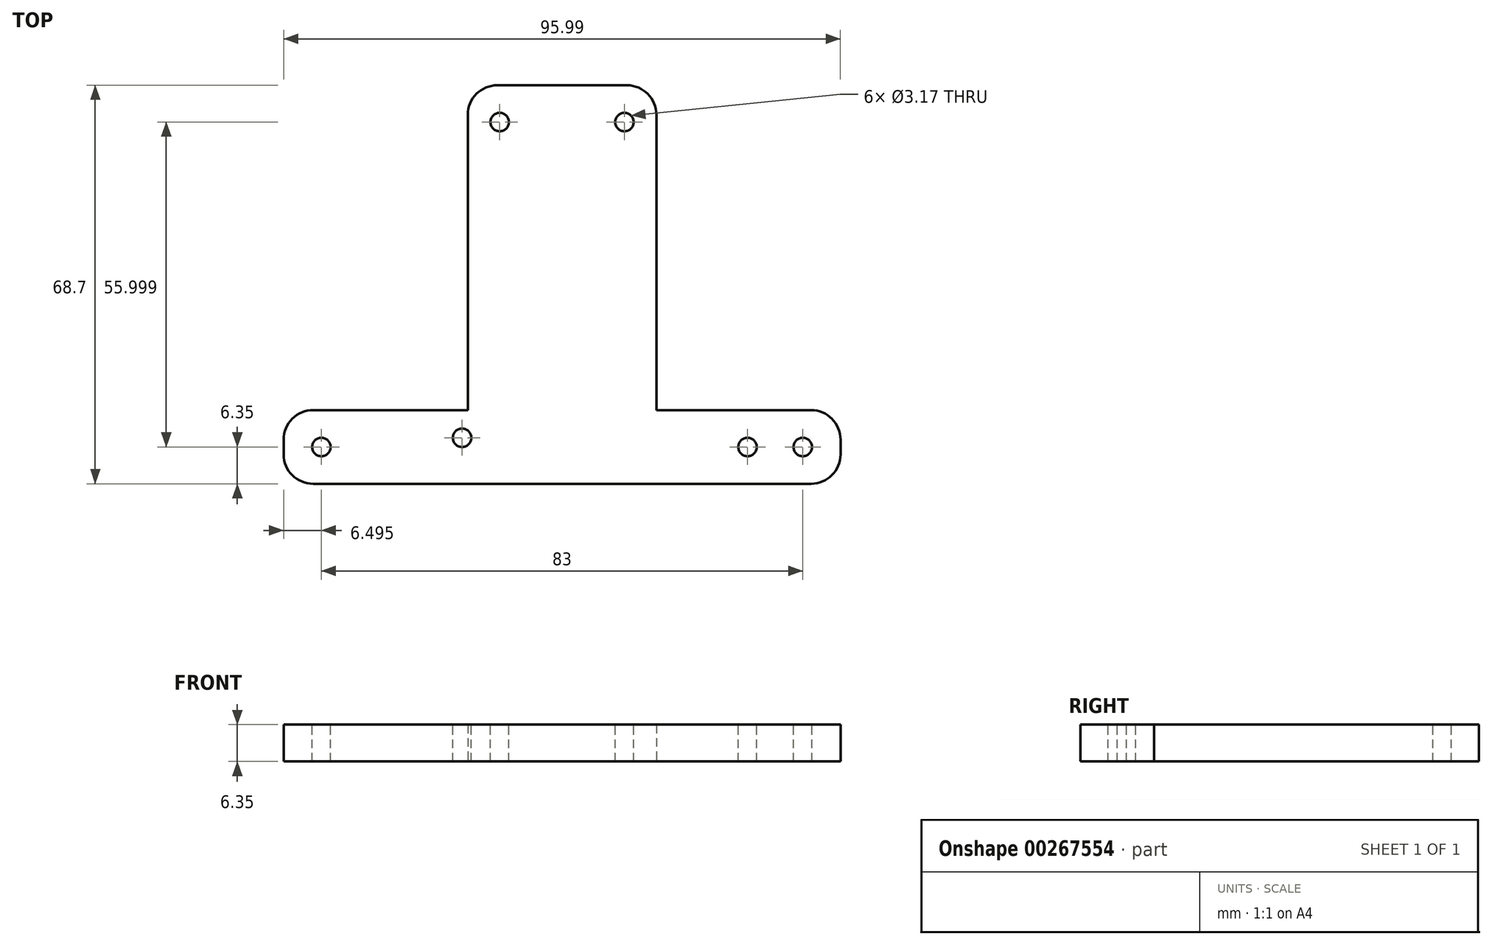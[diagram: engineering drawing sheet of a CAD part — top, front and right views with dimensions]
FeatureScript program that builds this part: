
annotation { "Feature Type Name" : "Feature", "Feature Type Description" : "" }
export const myFeature = defineFeature(function(context is Context, id is Id, definition is map)
    precondition{}
    {
        {
            var Q0;
            Q0=qCreatedBy(makeId("Top.planeOp"),FACE);
            var sketch = newSketch(context, id + "F0", { "sketchPlane" : qUnion([Q0])});
            skLineSegment(sketch, "E0.bottom", {"start": v(-48.42, 0) * mm, "end": v(47.57, 0) * mm});
            skLineSegment(sketch, "E0.top", {"start": v(-48.42, 12.7) * mm, "end": v(47.57, 12.7) * mm});
            skLineSegment(sketch, "E0.left", {"start": v(-48.42, 0) * mm, "end": v(-48.42, 12.7) * mm});
            skLineSegment(sketch, "E0.right", {"start": v(47.57, 0) * mm, "end": v(47.57, 12.7) * mm});
            skLineSegment(sketch, "E1.bottom", {"start": v(-16.67, 12.7) * mm, "end": v(15.82, 12.7) * mm});
            skLineSegment(sketch, "E1.top", {"start": v(-16.67, 68.7) * mm, "end": v(15.82, 68.7) * mm});
            skLineSegment(sketch, "E1.left", {"start": v(-16.67, 12.7) * mm, "end": v(-16.67, 68.7) * mm});
            skLineSegment(sketch, "E1.right", {"start": v(15.82, 12.7) * mm, "end": v(15.82, 68.7) * mm});
            skSolve(sketch);
        }
        {
            var Q0;
            Q0 = qSketchRegion(id + "F0", true);
            extrude(context, id + "F1", {"entities" : qUnion([Q0]), "depth" : 6.35 * mm});
        }
        {
            var Q0;
            Q0=makeQuery(id+"F1.opExtrude","CAP_FACE",FACE,{"disambiguationData":[OSD([sQuery(id+"F0.wireOp",EDGE,"E0.bottom"),sQuery(id+"F0.wireOp",EDGE,"E0.top"),sQuery(id+"F0.wireOp",EDGE,"E0.left"),sQuery(id+"F0.wireOp",EDGE,"E0.right"),sQuery(id+"F0.wireOp",EDGE,"E1.top"),sQuery(id+"F0.wireOp",EDGE,"E1.left"),sQuery(id+"F0.wireOp",EDGE,"E1.right")])],"isStart":false});
            var sketch = newSketch(context, id + "F2", { "sketchPlane" : qUnion([Q0])});
            skCircle(sketch, "E2", {"center": v(41.08, 6.35) * mm, "radius": 1.59 * mm});
            skCircle(sketch, "E3", {"center": v(-41.92, 6.35) * mm, "radius": 1.59 * mm});
            skCircle(sketch, "E4", {"center": v(-11.18, 62.35) * mm, "radius": 1.59 * mm});
            skCircle(sketch, "E5", {"center": v(10.33, 62.35) * mm, "radius": 1.59 * mm});
            skSolve(sketch);
        }
        {
            var Q0;
            Q0 = qSketchRegion(id + "F2", true);
            extrude(context, id + "F3", {"entities" : qUnion([Q0]), "operationType" : NewBodyOperationType.REMOVE, "oppositeDirection" : true, "depth" : 25.4 * mm});
        }
        {
            var Q0;
            Q0=makeQuery(id+"F1.opExtrude","SWEPT_EDGE",EDGE,{"disambiguationData":[OSD([sQuery(id+"F0.wireOp",EDGE,"E0.top"),sQuery(id+"F0.wireOp",EDGE,"E0.right")])]});
            var Q1;
            Q1=makeQuery(id+"F1.opExtrude","SWEPT_EDGE",EDGE,{"disambiguationData":[OSD([sQuery(id+"F0.wireOp",EDGE,"E0.bottom"),sQuery(id+"F0.wireOp",EDGE,"E0.right")])]});
            var Q2;
            Q2=makeQuery(id+"F1.opExtrude","SWEPT_EDGE",EDGE,{"disambiguationData":[OSD([sQuery(id+"F0.wireOp",EDGE,"E0.bottom"),sQuery(id+"F0.wireOp",EDGE,"E0.left")])]});
            var Q3;
            Q3=makeQuery(id+"F1.opExtrude","SWEPT_EDGE",EDGE,{"disambiguationData":[OSD([sQuery(id+"F0.wireOp",EDGE,"E0.top"),sQuery(id+"F0.wireOp",EDGE,"E0.left")])]});
            var Q4;
            Q4=makeQuery(id+"F1.opExtrude","SWEPT_EDGE",EDGE,{"disambiguationData":[OSD([sQuery(id+"F0.wireOp",EDGE,"E1.top"),sQuery(id+"F0.wireOp",EDGE,"E1.right")])]});
            var Q5;
            Q5=makeQuery(id+"F1.opExtrude","SWEPT_EDGE",EDGE,{"disambiguationData":[OSD([sQuery(id+"F0.wireOp",EDGE,"E1.top"),sQuery(id+"F0.wireOp",EDGE,"E1.left")])]});
            fillet(context, id + "F4", {"entities" : qUnion([Q0, Q1, Q2, Q3, Q4, Q5]), "radius" : 5.08 * mm, "tangentPropagation" : true, "allowEdgeOverflow" : false});
        }
        {
            var Q0;
            Q0=makeQuery(id+"F1.opExtrude","CAP_FACE",FACE,{"disambiguationData":[OSD([sQuery(id+"F0.wireOp",EDGE,"E0.bottom"),sQuery(id+"F0.wireOp",EDGE,"E0.top"),sQuery(id+"F0.wireOp",EDGE,"E0.left"),sQuery(id+"F0.wireOp",EDGE,"E0.right"),sQuery(id+"F0.wireOp",EDGE,"E1.top"),sQuery(id+"F0.wireOp",EDGE,"E1.left"),sQuery(id+"F0.wireOp",EDGE,"E1.right")])],"isStart":false});
            var sketch = newSketch(context, id + "F5", { "sketchPlane" : qUnion([Q0])});
            skCircle(sketch, "E6", {"center": v(31.55, 6.35) * mm, "radius": 1.59 * mm});
            skCircle(sketch, "E7", {"center": v(-17.66, 7.94) * mm, "radius": 1.59 * mm});
            skLineSegment(sketch, "E8", {"start": v(31.55, 6.35) * mm, "end": v(-31.22, 6.35) * mm});
            skLineSegment(sketch, "E9", {"start": v(-16.07, 7.94) * mm, "end": v(-16.07, 6.35) * mm});
            skSolve(sketch);
        }
        {
            var Q0;
            {var subQ0=sQuery(id+"F5.wireOp",EDGE,"E7");var subQ1=makeQuery(id+"F5.imprint","INTERSECT",VERTEX,{"derivedFrom":[subQ0,sQuery(id+"F5.wireOp",EDGE,"E9")]});Q0=makeQuery(id+"F5.imprint","IMPRINT",FACE,{"disambiguationData":[TD([[makeQuery(id+"F5.imprint","IMPRINT",EDGE,{"disambiguationData":[TD([[subQ1,-1.0]])],"derivedFrom":subQ0}),1.0]])]});}
            var Q1;
            Q1=makeQuery(id+"F5.imprint","IMPRINT",FACE,{"disambiguationData":[TD([[makeQuery(id+"F5.imprint","IMPRINT",EDGE,{"derivedFrom":sQuery(id+"F5.wireOp",EDGE,"E6")}),1.0]])]});
            var Q2;
            Q2=sQuery(id+"F5.wireOp",EDGE,"E7");
            var Q3;
            Q3=sQuery(id+"F5.wireOp",EDGE,"E6");
            extrude(context, id + "F6", {"entities" : qUnion([Q0, Q1]), "operationType" : NewBodyOperationType.REMOVE, "surfaceEntities" : qUnion([Q2, Q3]), "oppositeDirection" : true, "depth" : 25.4 * mm});
        }
    });
